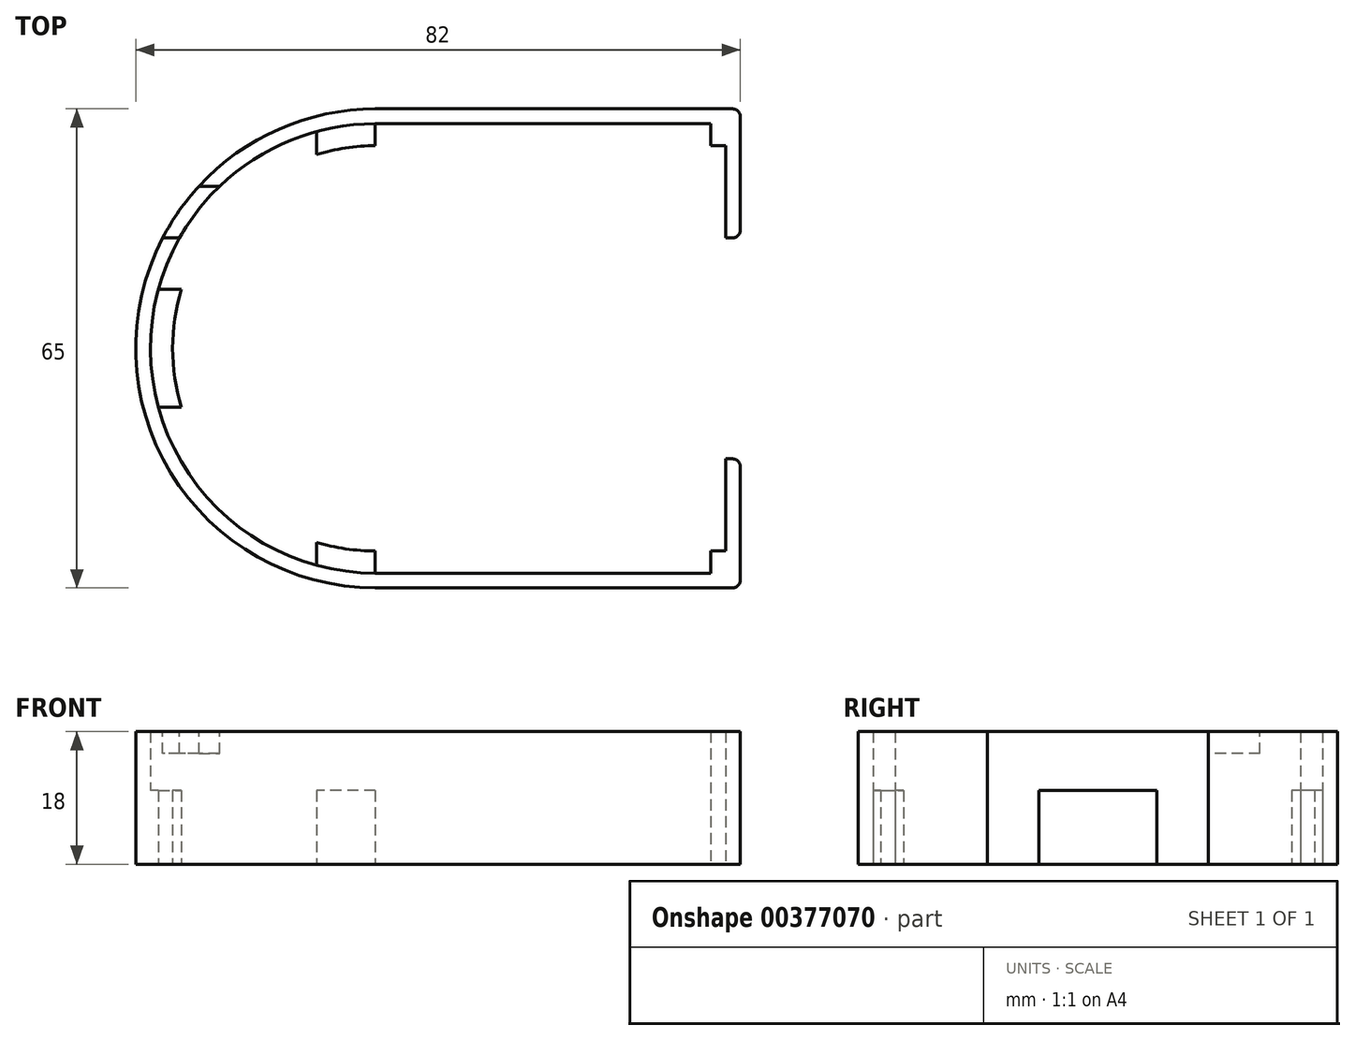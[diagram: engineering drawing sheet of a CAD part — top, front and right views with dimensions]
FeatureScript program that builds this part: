
annotation { "Feature Type Name" : "Feature", "Feature Type Description" : "" }
export const myFeature = defineFeature(function(context is Context, id is Id, definition is map)
    precondition{}
    {
        {
            var Q0;
            Q0=qCreatedBy(makeId("Top.planeOp"),FACE);
            var sketch = newSketch(context, id + "F0", { "sketchPlane" : qUnion([Q0])});
            skLineSegment(sketch, "E0.bottom", {"start": v(20, 15) * mm, "end": v(47.5, 15) * mm, "construction": true});
            skLineSegment(sketch, "E0.right", {"start": v(47.5, 15) * mm, "end": v(47.5, -15) * mm, "construction": true});
            skLineSegment(sketch, "E1", {"start": v(0, 0) * mm, "end": v(27.5, 0) * mm, "construction": true});
            skPoint(sketch, "E1.endSnap0", {"position": v(27.5, 0) * mm});
            skPoint(sketch, "E2.startSnap0", {"position": v(47.5, 0) * mm});
            skLineSegment(sketch, "E3", {"start": v(20, 15) * mm, "end": v(20, 15) * mm});
            skLineSegment(sketch, "E4", {"start": v(20, 15) * mm, "end": v(20, -15) * mm, "construction": true});
            skLineSegment(sketch, "E5", {"start": v(20, -15) * mm, "end": v(47.5, -15) * mm, "construction": true});
            skLineSegment(sketch, "E6", {"start": v(0, 32.5) * mm, "end": v(0, 32.5) * mm});
            skLineSegment(sketch, "E7", {"start": v(49.5, -15) * mm, "end": v(49.5, -32.5) * mm});
            skLineSegment(sketch, "E8", {"start": v(49.5, -32.5) * mm, "end": v(0, -32.5) * mm});
            skLineSegment(sketch, "E9", {"start": v(47.5, -15) * mm, "end": v(49.5, -15) * mm});
            skLineSegment(sketch, "E10", {"start": v(0, -32.5) * mm, "end": v(0, -32.5) * mm});
            skArc(sketch, "E11", {"start": v(0, -32.5) * mm, "mid": v(32.5, 0) * mm, "end": v(0, 32.5) * mm, "construction": true});
            skArc(sketch, "E12", {"start": v(0, 32.5) * mm, "mid": v(-32.5, 0) * mm, "end": v(0, -32.5) * mm});
            skLineSegment(sketch, "E13", {"start": v(0, -30.5) * mm, "end": v(0, -30.5) * mm});
            skLineSegment(sketch, "E14", {"start": v(0, 0) * mm, "end": v(-30.5, 0) * mm, "construction": true});
            skLineSegment(sketch, "E15", {"start": v(-30.5, 0) * mm, "end": v(-30.5, -8) * mm, "construction": true});
            skLineSegment(sketch, "E16", {"start": v(-30.5, -8) * mm, "end": v(-26.31, -8) * mm});
            skLineSegment(sketch, "E17.MirrorCS", {"start": v(49.5, 32.5) * mm, "end": v(0, 32.5) * mm});
            skLineSegment(sketch, "E18.MirrorCS", {"start": v(49.5, 15) * mm, "end": v(49.5, 32.5) * mm});
            skLineSegment(sketch, "E19.MirrorCS", {"start": v(47.5, 15) * mm, "end": v(49.5, 15) * mm});
            skLineSegment(sketch, "E20.MirrorCS", {"start": v(0, 30.5) * mm, "end": v(0, 30.5) * mm});
            skLineSegment(sketch, "E21.MirrorCS", {"start": v(-30.5, 8) * mm, "end": v(-26.31, 8) * mm});
            skLineSegment(sketch, "E22.MirrorCS", {"start": v(-30.5, 0) * mm, "end": v(-30.5, 8) * mm, "construction": true});
            skArc(sketch, "E23", {"start": v(-26.31, 8) * mm, "mid": v(-27.5, 0) * mm, "end": v(-26.31, -8) * mm});
            skArc(sketch, "E24", {"start": v(-26.31, -8) * mm, "mid": v(22.1, -16.37) * mm, "end": v(0, 27.5) * mm, "construction": true});
            skArc(sketch, "E25", {"start": v(0, 30.5) * mm, "mid": v(-18.52, 24.23) * mm, "end": v(-29.43, 8) * mm});
            skArc(sketch, "E26", {"start": v(0, -30.5) * mm, "mid": v(30.5, 0) * mm, "end": v(0, 30.5) * mm, "construction": true});
            skArc(sketch, "E27", {"start": v(-29.43, 8) * mm, "mid": v(-30.5, 0) * mm, "end": v(-29.43, -8) * mm});
            skArc(sketch, "E28", {"start": v(-29.43, -8) * mm, "mid": v(-18.52, -24.23) * mm, "end": v(0, -30.5) * mm});
            skLineSegment(sketch, "E29", {"start": v(47.5, -15) * mm, "end": v(47.5, -27.5) * mm});
            skLineSegment(sketch, "E30", {"start": v(47.5, -27.5) * mm, "end": v(45.5, -27.5) * mm});
            skLineSegment(sketch, "E31", {"start": v(45.5, -27.5) * mm, "end": v(45.5, -30.5) * mm});
            skLineSegment(sketch, "E32", {"start": v(0, -30.5) * mm, "end": v(45.5, -30.5) * mm});
            skLineSegment(sketch, "E33.MirrorCS", {"start": v(0, 30.5) * mm, "end": v(45.5, 30.5) * mm});
            skLineSegment(sketch, "E34.MirrorCS", {"start": v(45.5, 27.5) * mm, "end": v(45.5, 30.5) * mm});
            skLineSegment(sketch, "E35.MirrorCS", {"start": v(47.5, 27.5) * mm, "end": v(45.5, 27.5) * mm});
            skLineSegment(sketch, "E36.MirrorCS", {"start": v(47.5, 15) * mm, "end": v(47.5, 27.5) * mm});
            skLineSegment(sketch, "E37", {"start": v(0, 30.5) * mm, "end": v(0, 27.5) * mm});
            skLineSegment(sketch, "E38", {"start": v(0, 27.5) * mm, "end": v(-8, 27.5) * mm, "construction": true});
            skLineSegment(sketch, "E39", {"start": v(-8, 29.43) * mm, "end": v(-8, 26.31) * mm});
            skLineSegment(sketch, "E40", {"start": v(-8, 26.31) * mm, "end": v(-8, 26.31) * mm});
            skArc(sketch, "E41", {"start": v(0, 27.5) * mm, "mid": v(-4.04, 27.2) * mm, "end": v(-8, 26.31) * mm});
            skArc(sketch, "E42", {"start": v(-8, 26.31) * mm, "mid": v(-19.45, 19.45) * mm, "end": v(-26.31, 8) * mm, "construction": true});
            skLineSegment(sketch, "E43.MirrorCS", {"start": v(0, -30.5) * mm, "end": v(0, -27.5) * mm});
            skLineSegment(sketch, "E44.MirrorCS", {"start": v(-8, -29.43) * mm, "end": v(-8, -26.31) * mm});
            skArc(sketch, "E45.MirrorCS", {"start": v(0, -27.5) * mm, "mid": v(-4.04, -27.2) * mm, "end": v(-8, -26.31) * mm});
            skLineSegment(sketch, "E46", {"start": v(-26.31, 8) * mm, "end": v(-26.31, 15) * mm, "construction": true});
            skLineSegment(sketch, "E47", {"start": v(-26.31, 8) * mm, "end": v(-26.31, 22) * mm, "construction": true});
            skLineSegment(sketch, "E48", {"start": v(-26.31, 22) * mm, "end": v(-14.22, 22) * mm, "construction": true});
            skLineSegment(sketch, "E49", {"start": v(-26.31, 15) * mm, "end": v(-35.46, 15) * mm, "construction": true});
            skSolve(sketch);
        }
        {
            var Q0;
            Q0=makeQuery(id+"F0.imprint","IMPRINT",FACE,{"disambiguationData":[TD([[makeQuery(id+"F0.imprint","IMPRINT",EDGE,{"derivedFrom":sQuery(id+"F0.wireOp",EDGE,"E7")}),-1.0]])]});
            var Q1;
            {var subQ0=sQuery(id+"F0.wireOp",EDGE,"E48");var subQ1=sQuery(id+"F0.wireOp",EDGE,"E12");var subQ2=makeQuery(id+"F0.imprint","INTERSECT",VERTEX,{"derivedFrom":[subQ1,subQ0]});Q1=makeQuery(id+"F0.imprint","IMPRINT",FACE,{"disambiguationData":[TD([[makeQuery(id+"F0.imprint","IMPRINT",EDGE,{"disambiguationData":[TD([[subQ2,-1.0]])],"derivedFrom":subQ1}),1.0]])]});}
            var Q2;
            {var subQ0=sQuery(id+"F0.wireOp",EDGE,"E17.MirrorCS");Q2=makeQuery(id+"F0.imprint","IMPRINT",FACE,{"disambiguationData":[TD([[makeQuery(id+"F0.imprint","IMPRINT",EDGE,{"derivedFrom":subQ0}),1.0]])]});}
            extrude(context, id + "F1", {"entities" : qUnion([Q0, Q1, Q2]), "depth" : 18 * mm});
        }
        {
            var Q0;
            Q0=makeQuery(id+"F1.opExtrude","SWEPT_EDGE",EDGE,{"disambiguationData":[OSD([sQuery(id+"F0.wireOp",EDGE,"E18.MirrorCS"),sQuery(id+"F0.wireOp",EDGE,"E19.MirrorCS")])]});
            var Q1;
            Q1=makeQuery(id+"F1.opExtrude","SWEPT_EDGE",EDGE,{"disambiguationData":[OSD([sQuery(id+"F0.wireOp",EDGE,"E7"),sQuery(id+"F0.wireOp",EDGE,"E9")])]});
            var Q2;
            Q2=makeQuery(id+"F1.opExtrude","SWEPT_EDGE",EDGE,{"disambiguationData":[OSD([sQuery(id+"F0.wireOp",EDGE,"E17.MirrorCS"),sQuery(id+"F0.wireOp",EDGE,"E18.MirrorCS")])]});
            var Q3;
            Q3=makeQuery(id+"F1.opExtrude","SWEPT_EDGE",EDGE,{"disambiguationData":[OSD([sQuery(id+"F0.wireOp",EDGE,"E7"),sQuery(id+"F0.wireOp",EDGE,"E8")])]});
            fillet(context, id + "F2", {"entities" : qUnion([Q0, Q1, Q2, Q3]), "radius" : 1 * mm, "tangentPropagation" : true, "allowEdgeOverflow" : false});
        }
        {
            var Q0;
            {var subQ0=sQuery(id+"F0.wireOp",EDGE,"E37");Q0=makeQuery(id+"F0.imprint","IMPRINT",FACE,{"disambiguationData":[TD([[makeQuery(id+"F0.imprint","IMPRINT",EDGE,{"derivedFrom":subQ0}),-1.0]])]});}
            var Q1;
            {var subQ0=sQuery(id+"F0.wireOp",EDGE,"E23");Q1=makeQuery(id+"F0.imprint","IMPRINT",FACE,{"disambiguationData":[TD([[makeQuery(id+"F0.imprint","IMPRINT",EDGE,{"derivedFrom":subQ0}),-1.0]])]});}
            var Q2;
            {var subQ0=sQuery(id+"F0.wireOp",EDGE,"E43.MirrorCS");Q2=makeQuery(id+"F0.imprint","IMPRINT",FACE,{"disambiguationData":[TD([[makeQuery(id+"F0.imprint","IMPRINT",EDGE,{"derivedFrom":subQ0}),1.0]])]});}
            extrude(context, id + "F3", {"entities" : qUnion([Q0, Q1, Q2]), "operationType" : NewBodyOperationType.ADD, "depth" : 10 * mm});
        }
        {
            var Q0;
            Q0=makeQuery(id+"F1.opExtrude","CAP_FACE",FACE,{"disambiguationData":[OSD([sQuery(id+"F0.wireOp",EDGE,"E7"),sQuery(id+"F0.wireOp",EDGE,"E8"),sQuery(id+"F0.wireOp",EDGE,"E9"),sQuery(id+"F0.wireOp",EDGE,"E12"),sQuery(id+"F0.wireOp",EDGE,"E17.MirrorCS"),sQuery(id+"F0.wireOp",EDGE,"E18.MirrorCS"),sQuery(id+"F0.wireOp",EDGE,"E19.MirrorCS"),sQuery(id+"F0.wireOp",EDGE,"E25"),sQuery(id+"F0.wireOp",EDGE,"E27"),sQuery(id+"F0.wireOp",EDGE,"E28"),sQuery(id+"F0.wireOp",EDGE,"E30"),sQuery(id+"F0.wireOp",EDGE,"E31"),sQuery(id+"F0.wireOp",EDGE,"E32"),sQuery(id+"F0.wireOp",EDGE,"E29"),sQuery(id+"F0.wireOp",EDGE,"E33.MirrorCS"),sQuery(id+"F0.wireOp",EDGE,"E34.MirrorCS"),sQuery(id+"F0.wireOp",EDGE,"E35.MirrorCS"),sQuery(id+"F0.wireOp",EDGE,"E36.MirrorCS")])],"isStart":false});
            var sketch = newSketch(context, id + "F4", { "sketchPlane" : qUnion([Q0])});
            skLineSegment(sketch, "E50.0", {"start": v(-26.31, 15) * mm, "end": v(-35.46, 15) * mm});
            skLineSegment(sketch, "E50.1", {"start": v(-26.31, 22) * mm, "end": v(-14.22, 22) * mm});
            skSolve(sketch);
        }
        {
            var Q0;
            {var subQ0=sQuery(id+"F4.wireOp",EDGE,"E50.0");var subQ1=makeQuery(id+"F1.opExtrude","CAP_EDGE",EDGE,{"disambiguationData":[OSD([sQuery(id+"F0.wireOp",EDGE,"E12")])],"isStart":false});var subQ2=makeQuery(id+"F4.imprint","INTERSECT",VERTEX,{"derivedFrom":[subQ1,subQ0]});Q0=makeQuery(id+"F4.imprint","IMPRINT",FACE,{"disambiguationData":[TD([[makeQuery(id+"F4.imprint","IMPRINT",EDGE,{"disambiguationData":[TD([[subQ2,1.0]])],"derivedFrom":subQ1}),1.0]])]});}
            extrude(context, id + "F5", {"entities" : qUnion([Q0]), "operationType" : NewBodyOperationType.REMOVE, "oppositeDirection" : true, "depth" : 3 * mm});
        }
    });
